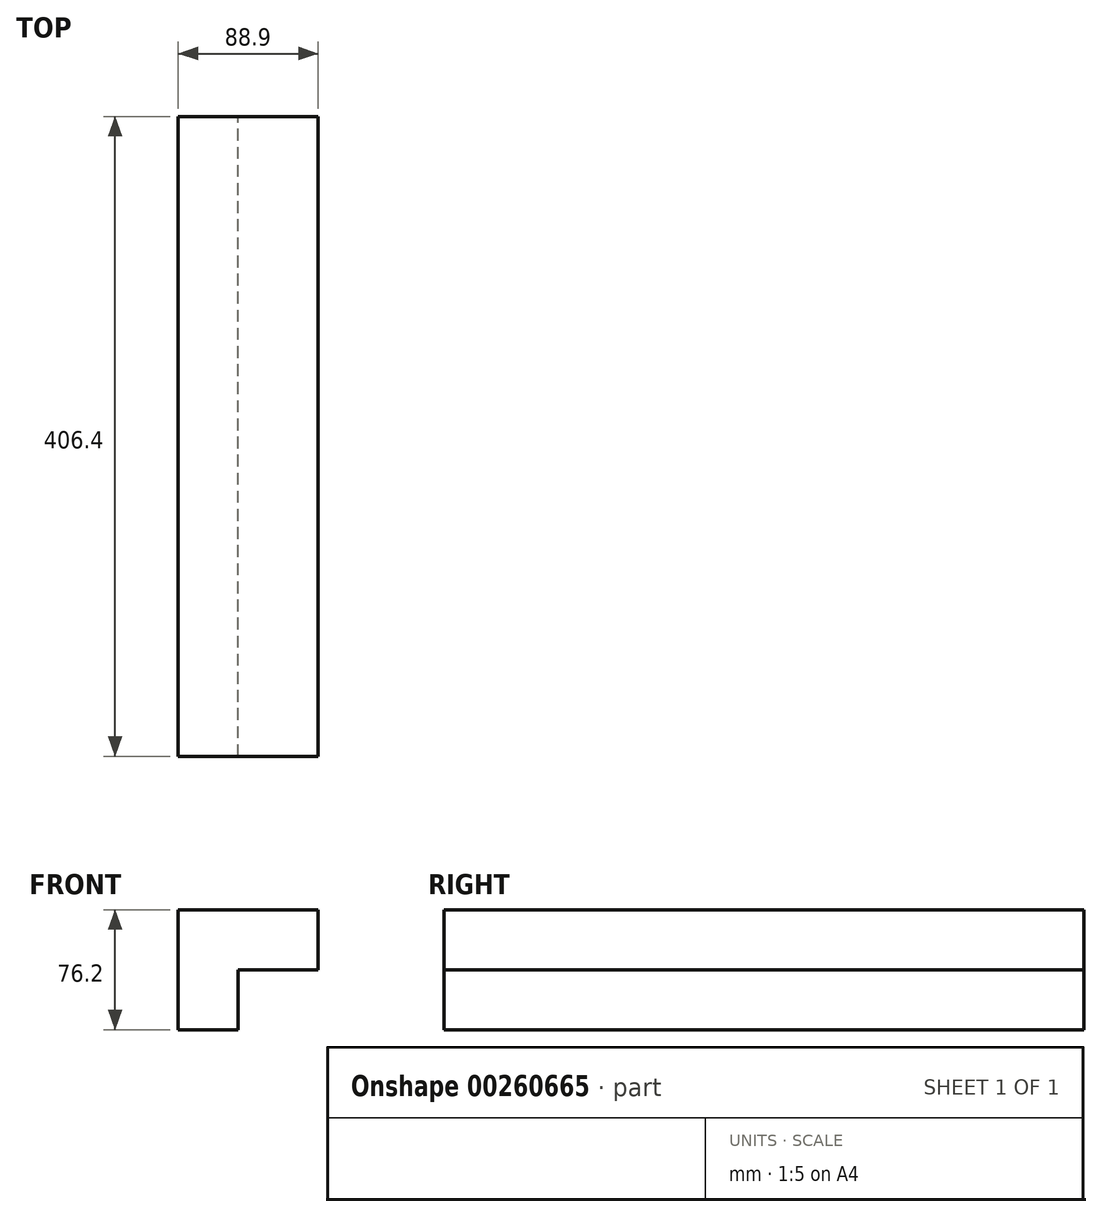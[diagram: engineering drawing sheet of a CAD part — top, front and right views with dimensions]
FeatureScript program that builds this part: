
annotation { "Feature Type Name" : "Feature", "Feature Type Description" : "" }
export const myFeature = defineFeature(function(context is Context, id is Id, definition is map)
    precondition{}
    {
        {
            var Q0;
            Q0=qCreatedBy(makeId("Front.planeOp"),FACE);
            var sketch = newSketch(context, id + "F0", { "sketchPlane" : qUnion([Q0])});
            skLineSegment(sketch, "E0", {"start": v(-52.28, 46.23) * mm, "end": v(-52.28, 8.13) * mm});
            skLineSegment(sketch, "E1", {"start": v(-52.28, 8.13) * mm, "end": v(36.62, 8.13) * mm});
            skLineSegment(sketch, "E2", {"start": v(36.62, 8.13) * mm, "end": v(36.62, 46.23) * mm});
            skLineSegment(sketch, "E3", {"start": v(36.62, 46.23) * mm, "end": v(-52.28, 46.23) * mm});
            skLineSegment(sketch, "E4", {"start": v(-52.28, 8.13) * mm, "end": v(-52.28, -29.97) * mm});
            skLineSegment(sketch, "E5", {"start": v(-52.28, -29.97) * mm, "end": v(-14.18, -29.97) * mm});
            skLineSegment(sketch, "E6", {"start": v(-14.18, -29.97) * mm, "end": v(-14.18, 8.13) * mm});
            skSolve(sketch);
        }
        {
            var Q0;
            {var subQ3=sQuery(id+"F0.wireOp",EDGE,"E0");Q0=makeQuery(id+"F0.imprint","IMPRINT",FACE,{"disambiguationData":[TD([[makeQuery(id+"F0.imprint","IMPRINT",EDGE,{"derivedFrom":subQ3}),1.0]])]});}
            var Q1;
            {var subQ0=sQuery(id+"F0.wireOp",EDGE,"E4");Q1=makeQuery(id+"F0.imprint","IMPRINT",FACE,{"disambiguationData":[TD([[makeQuery(id+"F0.imprint","IMPRINT",EDGE,{"derivedFrom":subQ0}),1.0]])]});}
            extrude(context, id + "F1", {"entities" : qUnion([Q0, Q1]), "depth" : 406.4 * mm});
        }
    });
